# Revit family: Electrical_Controls_Conspec_Primus-V-Ventilation-Controller
name_source: partatom
category: Electrical Fixtures
units: mm (PartAtom-declared; Revit-internal decimal feet)

## family parameters
Cut with Voids When Loaded = No
Host = Face
Maintain Annotation Orientation = No
OmniClass Number = 23.85.30.21
OmniClass Title = Environmental Detection/Registration
Part Type = Normal
Room Calculation Point = No
Round Connector Dimension = Use Diameter
Shared = No

## types (3) — shared parameters
Alarm = 4 custom alarm levels with off-delay timer, sensor Fail-High and Fail-Low alarms
Apparent Load = 0 VA
Assembly Code = D5030
Date Updated = 2023/10/17
Depth = 5.29 "
Description = PRIMUS V - CO and NO2 Detector for ventilation control in enclosed parking garages and other spaces subjected to toxic gases
Frequency = 0 Hz
Height = 9.04 "
Input/Output = 3 RS485 scan ports, 6 Relay outputs (5A@ 30VDC), 2 channels 4-20mA outputs
Keynote = 16000
Manufacturer = CONSPEC Controls
Maximum Current Consumption = 0 mA
Number of Poles = 3
Operating Humidity = 0% to 95% RH Non-Condesing
Operating Temperature = -4°F to +122°F
Power Factor = 0.8
Product Material = Conspec - Plastic - FR ABS - Grey
Product data url = https://bimobject.com
Software = Conspec Subcon Windows Software
URL = https://www.conspec-controls.com
Version = 1
Weight = 0.00 lbf
Width = 9.04 "
Zoning = Up to 12 programmable zones
zero-valued in all types: Default Elevation

## per-type parameters (varying)
| type | Voltage | Voltage Range | z_120 | z_DC |
| PRIMUS V - 24V DC | 24 V | 24V DC | No | Yes |
| PRIMUS V - 24V AC | 24 V | 24V AC | No | No |
| PRIMUS V - 120V AC | 120 V | 120V AC | Yes | No |

note: column(s) folded — value = type name in every type: Model

## geometry (parser evidence)
native form markers: Sweep x3
no freeform markers — native parametric forms only
